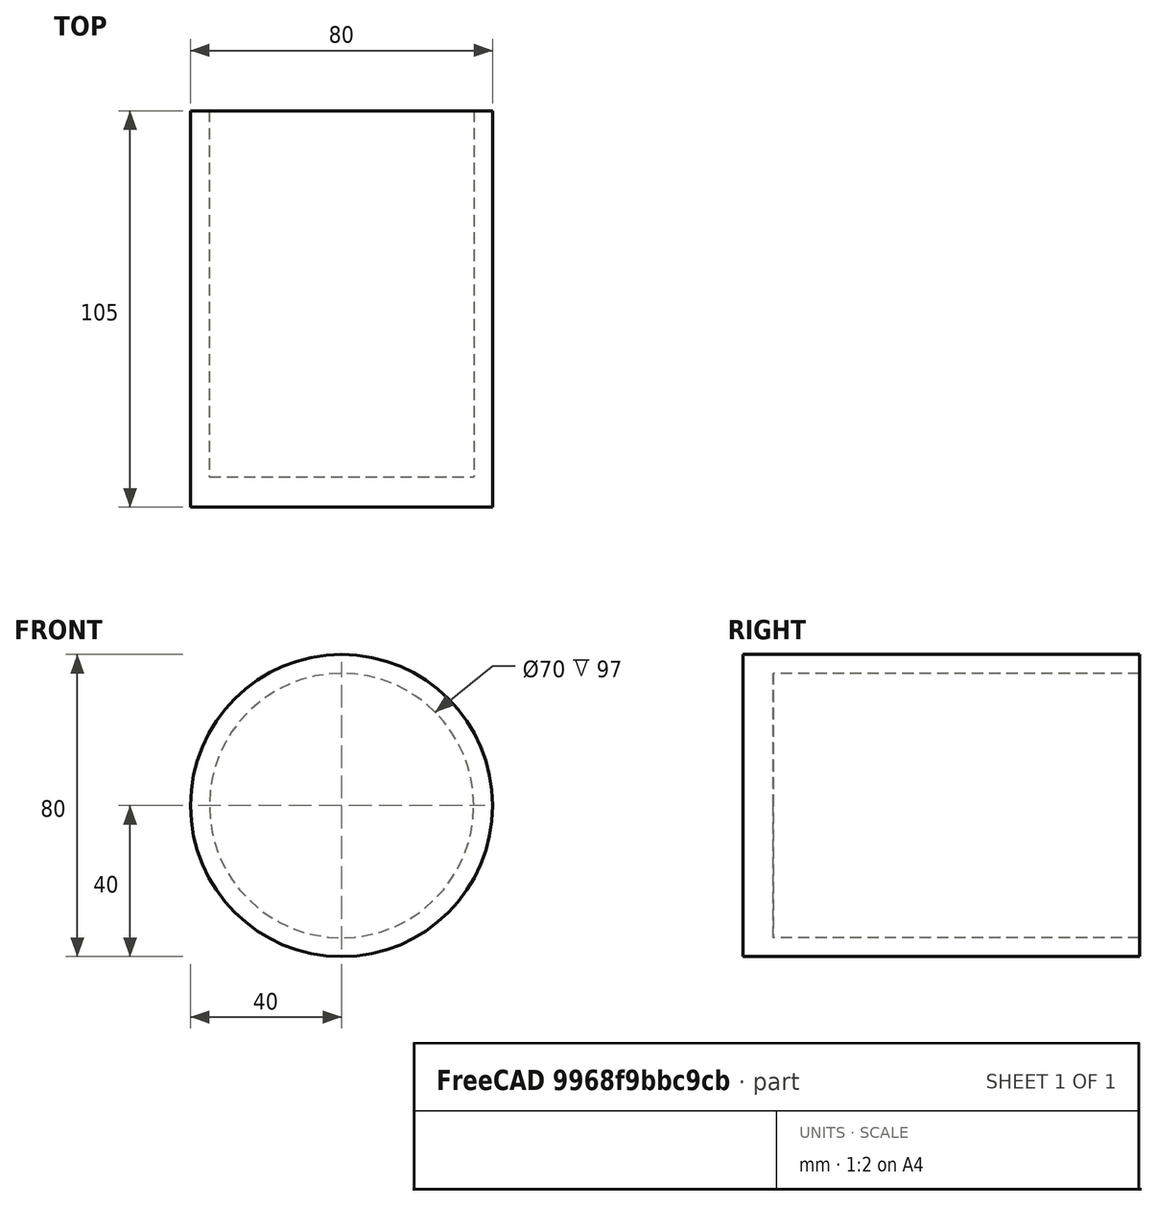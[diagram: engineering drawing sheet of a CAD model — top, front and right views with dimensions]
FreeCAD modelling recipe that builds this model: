
FCSTD DOCUMENT  (FreeCAD 0.20R29410 (Git))
Label: cup
License: All rights reserved
LicenseURL: http://en.wikipedia.org/wiki/All_rights_reserved
objects: Sketcher::SketchObject×1, PartDesign::Revolution×1, PartDesign::Body×1
note: 4 computed .brp shape members not serialized (recipe doc carries the construction recipe); baked Part::Feature solids carry a one-line shape summary decoded from their .brp

FEATURE [Sketcher::SketchObject] Sketch
  FullyConstrained = true
  MapMode = 5
  Support = -> [XY_Plane]
  sketch-geometry (6):
    g0: LineSegment StartX=-40 StartY=105 StartZ=0 EndX=-40 EndY=0 EndZ=0
    g1: LineSegment StartX=-35 StartY=105 StartZ=0 EndX=-35 EndY=8 EndZ=0
    g2: LineSegment StartX=-35 StartY=8 StartZ=0 EndX=0 EndY=8 EndZ=0
    g3: LineSegment StartX=-40 StartY=0 StartZ=0 EndX=0 EndY=0 EndZ=0
    g4: LineSegment StartX=-40 StartY=105 StartZ=0 EndX=-35 EndY=105 EndZ=0
    g5: LineSegment StartX=0 StartY=8 StartZ=0 EndX=0 EndY=0 EndZ=0
  constraints (17):
    c: Horizontal(g3)
    c: Coincident(g-1,g3)
    c: PointOnObject(g2,g-2)
    c: Parallel(g2,g3)
    c: Distance(g3,g2) = 8
    c: Distance(g3) = 40
    c: Distance(g2) = 35
    c: Coincident(g1,g2)
    c: Parallel(g1,g-2)
    c: Distance(g1) = 97
    c: Coincident(g0,g3)
    c: Parallel(g0,g-2)
    c: Distance(g0) = 105
    c: Coincident(g4,g1)
    c: Coincident(g4,g0)
    c: Coincident(g5,g2)
    c: Coincident(g5,g3)
FEATURE [PartDesign::Revolution] Revolution
  Angle = 360
  Axis = (0,1,0)
  Base = (0,0,0)
  Profile = -> Sketch
  ReferenceAxis = -> Sketch [V_Axis]
FEATURE [PartDesign::Body] Body
  Group = -> [Sketch,Revolution]
  Origin = -> Origin
  Tip = -> Revolution
